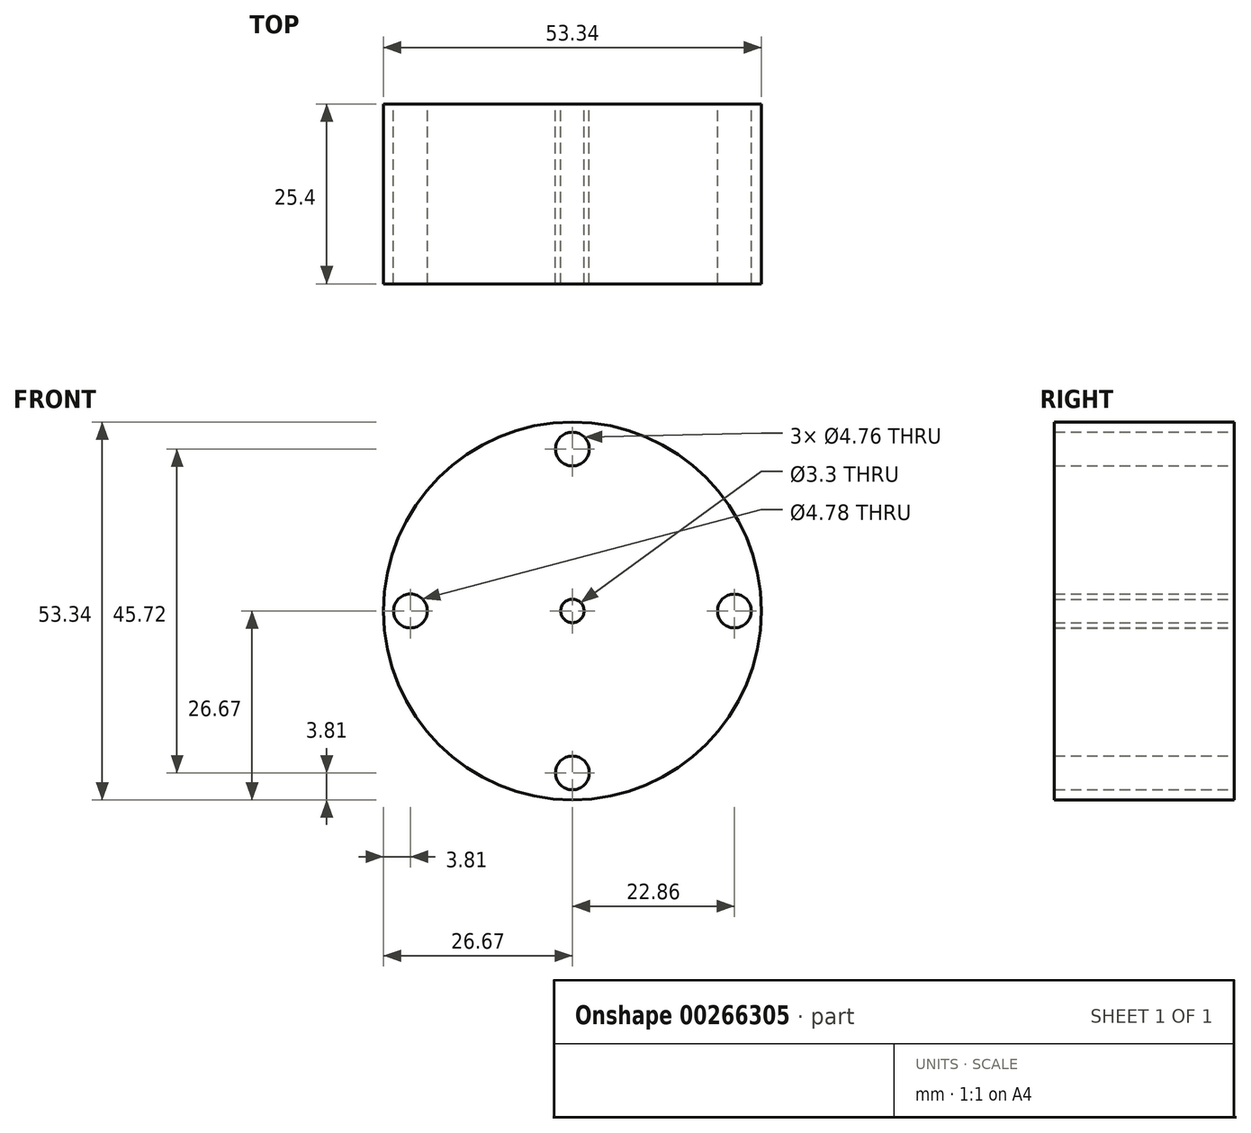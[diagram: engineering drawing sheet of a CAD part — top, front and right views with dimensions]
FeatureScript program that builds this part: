
annotation { "Feature Type Name" : "Feature", "Feature Type Description" : "" }
export const myFeature = defineFeature(function(context is Context, id is Id, definition is map)
    precondition{}
    {
        {
            var Q0;
            Q0=qCreatedBy(makeId("Front.planeOp"),FACE);
            var sketch = newSketch(context, id + "F0", { "sketchPlane" : qUnion([Q0])});
            skCircle(sketch, "E0", {"center": v(0, 0) * mm, "radius": 26.67 * mm});
            skCircle(sketch, "E1", {"center": v(0, 0) * mm, "radius": 1.65 * mm});
            skCircle(sketch, "E2", {"center": v(0, 22.86) * mm, "radius": 2.38 * mm});
            skCircle(sketch, "E3", {"center": v(22.86, 0) * mm, "radius": 2.38 * mm});
            skCircle(sketch, "E4", {"center": v(0, -22.86) * mm, "radius": 2.38 * mm});
            skCircle(sketch, "E5", {"center": v(-22.86, 0) * mm, "radius": 2.39 * mm});
            skSolve(sketch);
        }
        {
            var Q0;
            Q0=makeQuery(id+"F0.imprint","IMPRINT",FACE,{"disambiguationData":[TD([[makeQuery(id+"F0.imprint","IMPRINT",EDGE,{"derivedFrom":sQuery(id+"F0.wireOp",EDGE,"E0")}),1.0]])]});
            extrude(context, id + "F1", {"entities" : qUnion([Q0]), "depth" : 25.4 * mm});
        }
    });
